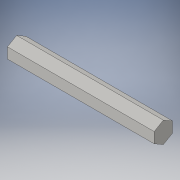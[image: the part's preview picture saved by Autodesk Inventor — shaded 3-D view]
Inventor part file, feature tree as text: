
AUTODESK INVENTOR PART (.ipt)
format: ipt  version: 2016 (Build 200138000, 138)  size: 89,088 bytes
history: native  units: in
note: dims shown in document units (in); Inventor stores cm internally (conversion verified against a paired STEP export)
features: extrude x1, sketch x1
ambient origin geometry x8: Origin, YZ Plane, XZ Plane, XY Plane, X Axis, Y Axis, Z Axis, Center Point
bodies: Solid1 (feature_tree)
feature tree (2):
  extrude  "Extrusion1"  Depth=3.0in TaperAngle=0.0deg
  sketch  "Sketch1"  dims[d0=0.375in d1=3.0in d2=0.0in]
